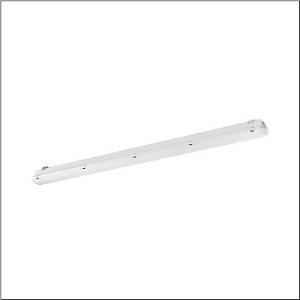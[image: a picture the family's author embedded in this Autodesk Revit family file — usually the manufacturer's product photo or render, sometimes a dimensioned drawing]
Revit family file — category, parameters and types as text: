
# Revit family: monsun_r__11xtreme_mo_51fe10mp480r_a813
name_source: partatom
category: Lighting Fixtures
units: mm (PartAtom-declared; Revit-internal decimal feet)

## family parameters
Cut with Voids When Loaded = No
Host = Face
Light Source = No
Part Type = Normal
Room Calculation Point = No
Round Connector Dimension = Use Diameter
Shared = No

## types (1)
- --- (1 x LED, 8000 lm, 43.2 W, 4000K)
    Apparent Load = 43 VA
    CIE Flux Codes = 47 77 93 94 100
    Color Rendering = 80
    Color Temperature = 4000K
    Default Elevation = 1800 mm
    Description = Monsun® 11Xtreme MO, damp-proof luminaire, chain hanger, primary optical cover: enclosure, of PMMA, light emission: direct distribution, primary light characteristic: symmetric, installation type: suspended mounting, surface-mounted, horizontal mounting, vertical mounting, LED, rated luminous flux: 8.000lm, luminous efficacy: 181lm/W, light colour: 840, colour temperature: 4000K, control gear: ECG, with terminal, 3-pole, max. 2.5mm², mains connection: 220..240V, AC, 50/60Hz, rated input power: 44W, luminaire housing, of glass-fibre reinforced polyester, uncoated, bright grey, length: 1.590mm, width: 90mm, height: 88mm, clip for enclosure, of stainless steel (V2A), ceiling mounting element, of stainless steel (V2A), chain hanger, of stainless steel (V2A), protection rating (complete): IP66, insulation class (complete): insulation class I (protective earthing), certification: CE, ENEC, VDE, UKCA, protection symbol: D, impact resistance: IK04, permissible operating ambient temperature: -35..+55°C (at 8000lm) / 60°C (at 4100lm), standard: EN 50419, EN 60598-2-1, corresponds to IFS (International Featured Standards) requirements for safety and quality in the food industry, for indoor or canopied outdoor use, no direct snow, no direct sun, no direct rain, packaging unit: 1 piece
    Height = 88 mm
    Lamp = 1 x LED
    Lamp Light Flux = 8000 lm
    Lamp Power = 43.2 W
    Lamp count = 1
    Length = 1590 mm
    Luminous efficacy = 185 lm/W
    Manufacturer = Siteco
    ModVariant = No
    Model = 51FE10MP480R
    Mounting Place = Ceiling
    Mounting Type = Pendant
    Number of Poles = 1
    OnlyDefault = Yes
    Power Factor = 1
    Product Name = Monsun® 11Xtreme MO
    Product group = damp-proof luminaire | ceiling pendant
    ProductGroupID = 908
    Protection Class = Protection class I
    Protection Degree = IP 66
    RLX_Detail_Level = 1
    RlxData = <blob elided: 85017 chars, md5=d1b89332>
    Socket = socket
    Standby Power = 0 W
    System Light Flux = 8000 lm
    System Power = 43 W
    Type Comments = factory setting: luminous flux: 100 % | (A | C | E) | 101 mA
    Type Image = l_1006851.jpg
    URL = http://relux.com
    VarID = @adj_112641
    Voltage = 0 V
    Weight = 0.00 kg
    Width = 90 mm

## geometry (parser evidence)
native form markers: Blend x4, Sweep x12
no freeform markers — native parametric forms only
